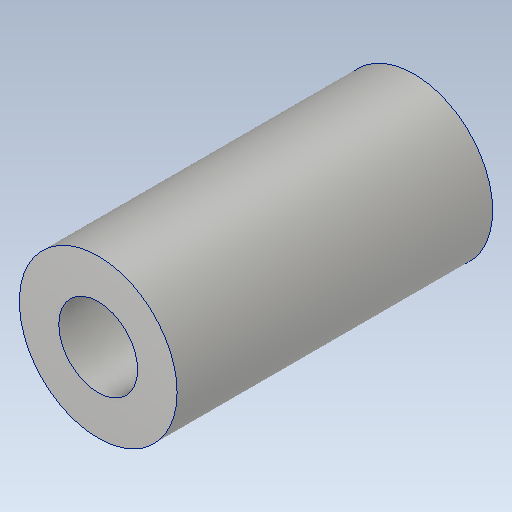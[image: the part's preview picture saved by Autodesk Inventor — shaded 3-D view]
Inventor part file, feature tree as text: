
AUTODESK INVENTOR PART (.ipt)
format: ipt  version: 2020.2 (Build 242310000, 310)  size: 108,032 bytes
history: native  units: mm
features: other x1, extrude x1, sketch x1
ambient origin geometry x8: Origin, YZ Plane, XZ Plane, XY Plane, X Axis, Y Axis, Z Axis, Center Point
bodies: Body1 (feature_tree)
feature tree (3):
  other  "ソリッド1"
  extrude  "押し出し1"  Depth=6.0mm
  sketch  "スケッチ1"
